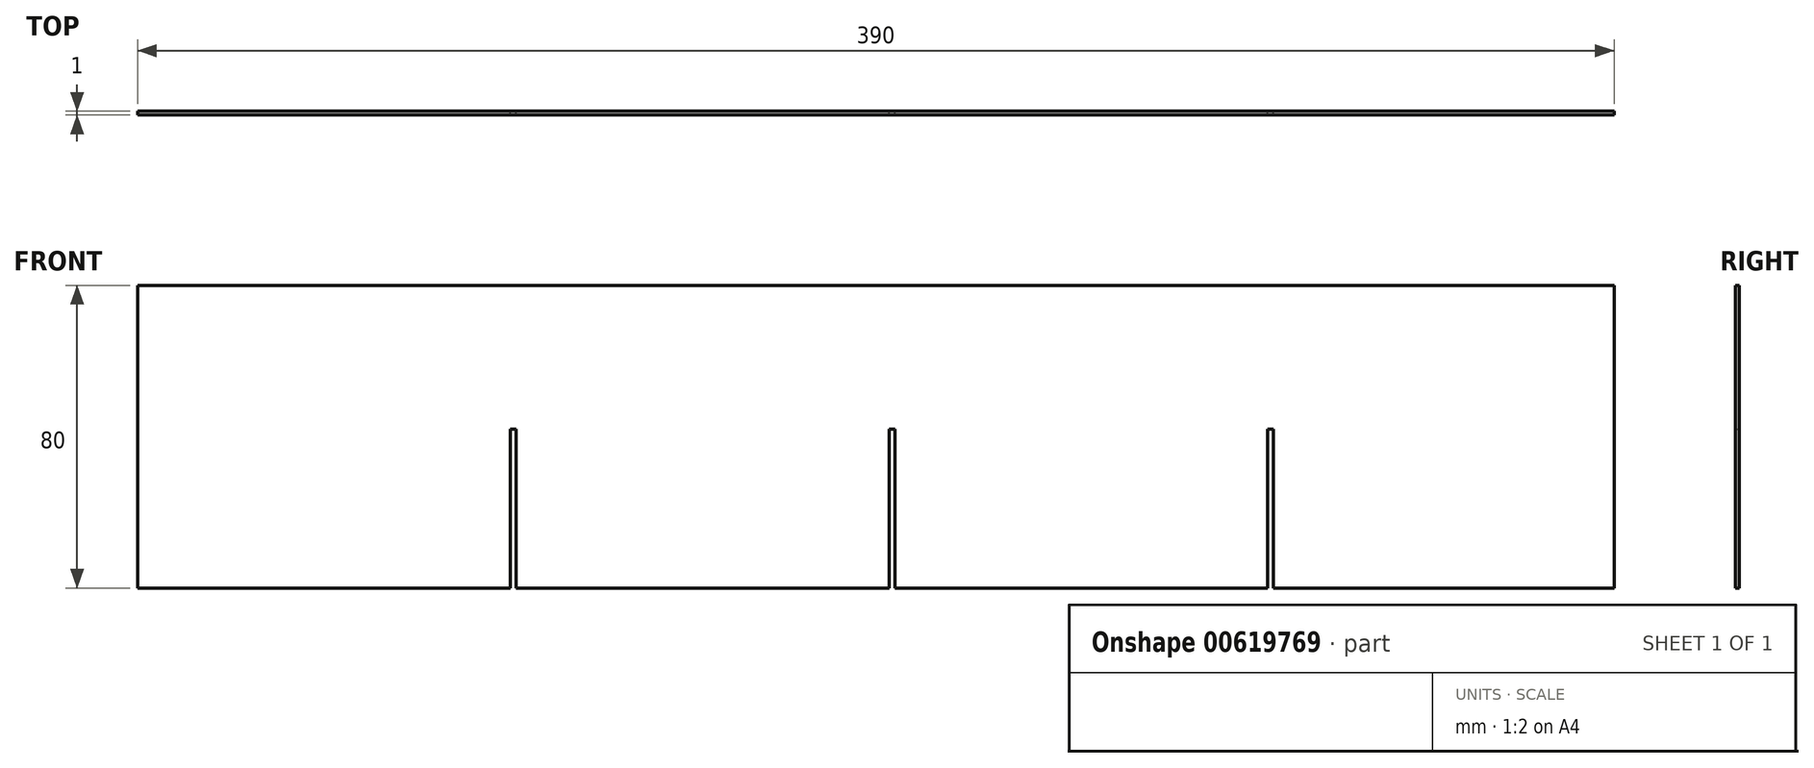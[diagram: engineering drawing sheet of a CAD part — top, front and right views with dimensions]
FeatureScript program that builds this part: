
annotation { "Feature Type Name" : "Feature", "Feature Type Description" : "" }
export const myFeature = defineFeature(function(context is Context, id is Id, definition is map)
    precondition{}
    {
        {
            var Q0;
            Q0=qCreatedBy(makeId("Front.planeOp"),FACE);
            var sketch = newSketch(context, id + "F0", { "sketchPlane" : qUnion([Q0])});
            skLineSegment(sketch, "E0", {"start": v(-67.02, -9.71) * mm, "end": v(31.48, -9.71) * mm});
            skLineSegment(sketch, "E1", {"start": v(31.48, -9.71) * mm, "end": v(31.48, 32.29) * mm});
            skLineSegment(sketch, "E2", {"start": v(31.48, 32.29) * mm, "end": v(32.98, 32.29) * mm});
            skLineSegment(sketch, "E3", {"start": v(32.98, 32.29) * mm, "end": v(32.98, -9.71) * mm});
            skLineSegment(sketch, "E4", {"start": v(32.98, -9.71) * mm, "end": v(131.48, -9.71) * mm});
            skLineSegment(sketch, "E5", {"start": v(131.48, -9.71) * mm, "end": v(131.48, 32.29) * mm});
            skLineSegment(sketch, "E6", {"start": v(131.48, 32.29) * mm, "end": v(132.98, 32.29) * mm});
            skLineSegment(sketch, "E7", {"start": v(132.98, 32.29) * mm, "end": v(132.98, -9.71) * mm});
            skLineSegment(sketch, "E8", {"start": v(132.98, -9.71) * mm, "end": v(231.48, -9.71) * mm});
            skLineSegment(sketch, "E9", {"start": v(231.48, -9.71) * mm, "end": v(231.48, 32.29) * mm});
            skLineSegment(sketch, "E10", {"start": v(231.48, 32.29) * mm, "end": v(232.98, 32.29) * mm});
            skLineSegment(sketch, "E11", {"start": v(232.98, 32.29) * mm, "end": v(232.98, -9.71) * mm});
            skLineSegment(sketch, "E12", {"start": v(-67.02, -9.71) * mm, "end": v(-67.02, 70.29) * mm});
            skLineSegment(sketch, "E13", {"start": v(-67.02, 70.29) * mm, "end": v(322.98, 70.29) * mm});
            skLineSegment(sketch, "E14", {"start": v(232.98, -9.71) * mm, "end": v(322.98, -9.71) * mm});
            skLineSegment(sketch, "E15", {"start": v(322.98, 70.29) * mm, "end": v(322.98, -9.71) * mm});
            skSolve(sketch);
        }
        {
            var Q0;
            Q0=makeQuery(id+"F0.imprint","IMPRINT",FACE,{"disambiguationData":[TD([[makeQuery(id+"F0.imprint","IMPRINT",EDGE,{"derivedFrom":sQuery(id+"F0.wireOp",EDGE,"E0")}),1.0]])]});
            extrude(context, id + "F1", {"entities" : qUnion([Q0]), "depth" : 1 * mm, "offsetDistance" : 25 * mm});
        }
    });
